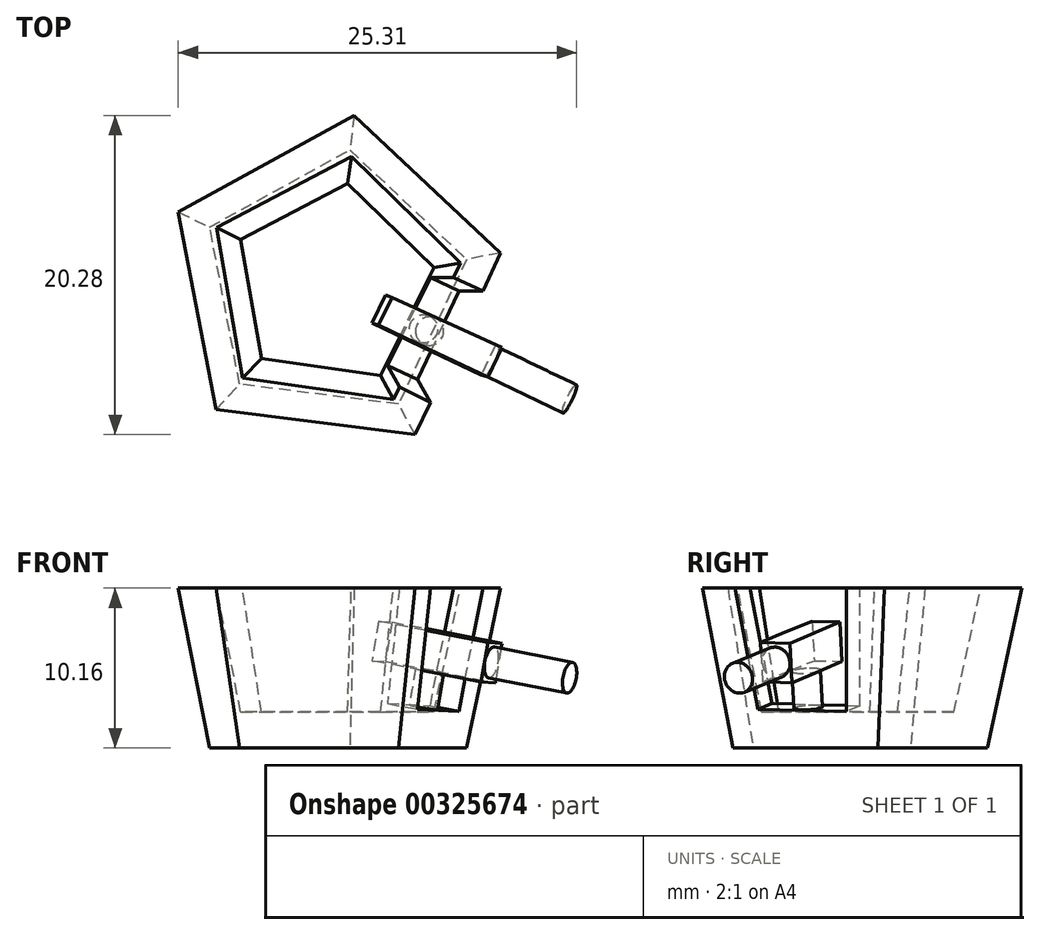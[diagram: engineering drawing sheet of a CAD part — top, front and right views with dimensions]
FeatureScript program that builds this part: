
annotation { "Feature Type Name" : "Feature", "Feature Type Description" : "" }
export const myFeature = defineFeature(function(context is Context, id is Id, definition is map)
    precondition{}
    {
        {
            var Q0;
            Q0=qCreatedBy(makeId("Top.planeOp"),FACE);
            var sketch = newSketch(context, id + "F0", { "sketchPlane" : qUnion([Q0])});
            skCircle(sketch, "E0.cCircle", {"center": v(0, 0) * mm, "radius": 7 * mm, "construction": true});
            skLineSegment(sketch, "E0.0", {"start": v(-7.82, 3.68) * mm, "end": v(1.08, 8.57) * mm});
            skLineSegment(sketch, "E0.1", {"start": v(1.08, 8.57) * mm, "end": v(8.49, 1.62) * mm});
            skLineSegment(sketch, "E0.2", {"start": v(8.49, 1.62) * mm, "end": v(4.17, -7.57) * mm});
            skLineSegment(sketch, "E0.3", {"start": v(4.17, -7.57) * mm, "end": v(-5.91, -6.3) * mm});
            skLineSegment(sketch, "E0.4", {"start": v(-5.91, -6.3) * mm, "end": v(-7.82, 3.68) * mm});
            skPoint(sketch, "E0.0.midPoint", {"position": v(-3.37, 6.13) * mm});
            skSolve(sketch);
        }
        {
            var Q0;
            Q0=makeQuery(id+"F0.imprint","IMPRINT",FACE,{"disambiguationData":[TD([[makeQuery(id+"F0.imprint","IMPRINT",EDGE,{"derivedFrom":sQuery(id+"F0.wireOp",EDGE,"E0.0")}),-1.0]])]});
            extrude(context, id + "F1", {"entities" : qUnion([Q0]), "depth" : 10.16 * mm, "hasDraft" : true, "draftAngle" : 10 * degree});
        }
        {
            var Q0;
            Q0=makeQuery(id+"F1.opExtrude","CAP_FACE",FACE,{"disambiguationData":[OSD([sQuery(id+"F0.wireOp",EDGE,"E0.0"),sQuery(id+"F0.wireOp",EDGE,"E0.1"),sQuery(id+"F0.wireOp",EDGE,"E0.2"),sQuery(id+"F0.wireOp",EDGE,"E0.3"),sQuery(id+"F0.wireOp",EDGE,"E0.4")])],"isStart":false});
            var sketch = newSketch(context, id + "F2", { "sketchPlane" : qUnion([Q0])});
            skCircle(sketch, "E1.cCircle", {"center": v(0, 0) * mm, "radius": 6.66 * mm, "construction": true});
            skLineSegment(sketch, "E1.0", {"start": v(1.17, 8.15) * mm, "end": v(8.11, 1.4) * mm});
            skLineSegment(sketch, "E1.1", {"start": v(8.11, 1.4) * mm, "end": v(3.84, -7.28) * mm});
            skLineSegment(sketch, "E1.2", {"start": v(3.84, -7.28) * mm, "end": v(-5.74, -5.9) * mm});
            skLineSegment(sketch, "E1.3", {"start": v(-5.74, -5.9) * mm, "end": v(-7.39, 3.63) * mm});
            skLineSegment(sketch, "E1.4", {"start": v(-7.39, 3.63) * mm, "end": v(1.17, 8.15) * mm});
            skPoint(sketch, "E1.0.midPoint", {"position": v(4.64, 4.78) * mm});
            skSolve(sketch);
        }
        {
            var Q0;
            Q0=makeQuery(id+"F2.imprint","IMPRINT",FACE,{"disambiguationData":[TD([[makeQuery(id+"F2.imprint","IMPRINT",EDGE,{"derivedFrom":sQuery(id+"F2.wireOp",EDGE,"E1.0")}),-1.0]])]});
            extrude(context, id + "F3", {"entities" : qUnion([Q0]), "operationType" : NewBodyOperationType.REMOVE, "oppositeDirection" : true, "depth" : 7.87 * mm, "hasDraft" : true, "draftAngle" : 10 * degree, "draftPullDirection" : true});
        }
        {
            var Q0;
            Q0=makeQuery(id+"F1.opExtrude","SWEPT_FACE",FACE,{"disambiguationData":[OSD([sQuery(id+"F0.wireOp",EDGE,"E0.2")])]});
            var sketch = newSketch(context, id + "F4", { "sketchPlane" : qUnion([Q0])});
            skLineSegment(sketch, "E2", {"start": v(-5.64, 13.98) * mm, "end": v(-3.44, 3.45) * mm});
            skLineSegment(sketch, "E3", {"start": v(-3.44, 3.45) * mm, "end": v(2.76, 3.83) * mm});
            skLineSegment(sketch, "E4", {"start": v(2.76, 3.83) * mm, "end": v(2.76, 14.1) * mm});
            skLineSegment(sketch, "E5", {"start": v(2.76, 14.1) * mm, "end": v(-5.64, 13.98) * mm});
            skSolve(sketch);
        }
        {
            var Q0;
            {var subQ0=sQuery(id+"F4.wireOp",EDGE,"E3");Q0=makeQuery(id+"F4.imprint","IMPRINT",FACE,{"disambiguationData":[TD([[makeQuery(id+"F4.imprint","IMPRINT",EDGE,{"derivedFrom":subQ0}),1.0]])]});}
            extrude(context, id + "F5", {"entities" : qUnion([Q0]), "operationType" : NewBodyOperationType.REMOVE, "oppositeDirection" : true, "depth" : 9.9 * mm});
        }
        {
            var Q0;
            Q0=makeQuery(id+"F5.boolean.opBoolean","COPY",FACE,{"derivedFrom":makeQuery(id+"F5.opExtrude","SWEPT_FACE",FACE,{"disambiguationData":[OSD([sQuery(id+"F4.wireOp",EDGE,"E3")])]})});
            var sketch = newSketch(context, id + "F6", { "sketchPlane" : qUnion([Q0])});
            skCircle(sketch, "E6", {"center": v(5.22, -2.65) * mm, "radius": 0.9 * mm});
            skSolve(sketch);
        }
        {
            var Q0;
            Q0=makeQuery(id+"F6.imprint","IMPRINT",FACE,{"disambiguationData":[TD([[makeQuery(id+"F6.imprint","IMPRINT",EDGE,{"derivedFrom":sQuery(id+"F6.wireOp",EDGE,"E6")}),1.0]])]});
            extrude(context, id + "F7", {"entities" : qUnion([Q0]), "operationType" : NewBodyOperationType.ADD, "depth" : 2.36 * mm});
        }
        {
            var Q0;
            Q0=makeQuery(id+"F7.opExtrude","CAP_FACE",FACE,{"disambiguationData":[OSD([sQuery(id+"F6.wireOp",EDGE,"E6")])],"isStart":false});
            var sketch = newSketch(context, id + "F8", { "sketchPlane" : qUnion([Q0])});
            skLineSegment(sketch, "E7", {"start": v(4.73, -3.66) * mm, "end": v(1.52, -2.1) * mm});
            skLineSegment(sketch, "E8", {"start": v(1.52, -2.1) * mm, "end": v(2.37, -0.34) * mm});
            skLineSegment(sketch, "E9", {"start": v(2.37, -0.34) * mm, "end": v(9.45, -3.6) * mm});
            skLineSegment(sketch, "E10", {"start": v(9.45, -3.6) * mm, "end": v(8.55, -5.46) * mm});
            skLineSegment(sketch, "E11", {"start": v(8.55, -5.46) * mm, "end": v(4.73, -3.66) * mm});
            skSolve(sketch);
        }
        {
            var Q0;
            {var subQ0=sQuery(id+"F8.wireOp",EDGE,"E9");var subQ1=makeQuery(id+"F7.opExtrude","CAP_EDGE",EDGE,{"disambiguationData":[OSD([sQuery(id+"F6.wireOp",EDGE,"E6")])],"isStart":false});var subQ2=makeQuery(id+"F8.imprint","INTERSECT",VERTEX,{"disambiguationData":[OD(0.0)],"derivedFrom":[subQ1,subQ0]});Q0=makeQuery(id+"F8.imprint","IMPRINT",FACE,{"disambiguationData":[TD([[makeQuery(id+"F8.imprint","IMPRINT",EDGE,{"disambiguationData":[TD([[subQ2,-1.0]])],"derivedFrom":subQ0}),-1.0]])]});}
            var Q1;
            Q1=makeQuery(id+"F8.imprint","IMPRINT",FACE,{"disambiguationData":[TD([[makeQuery(id+"F8.imprint","IMPRINT",EDGE,{"derivedFrom":sQuery(id+"F8.wireOp",EDGE,"E7")}),-1.0]])]});
            extrude(context, id + "F9", {"entities" : qUnion([Q0, Q1]), "operationType" : NewBodyOperationType.ADD, "depth" : 2.54 * mm});
        }
        {
            var Q0;
            Q0=makeQuery(id+"F9.opExtrude","SWEPT_FACE",FACE,{"disambiguationData":[OSD([sQuery(id+"F8.wireOp",EDGE,"E10")])]});
            var sketch = newSketch(context, id + "F10", { "sketchPlane" : qUnion([Q0])});
            skCircle(sketch, "E12", {"center": v(-0.62, 7.27) * mm, "radius": 1 * mm});
            skSolve(sketch);
        }
        {
            var Q0;
            Q0=makeQuery(id+"F10.imprint","IMPRINT",FACE,{"disambiguationData":[TD([[makeQuery(id+"F10.imprint","IMPRINT",EDGE,{"derivedFrom":sQuery(id+"F10.wireOp",EDGE,"E12")}),1.0]])]});
            extrude(context, id + "F11", {"entities" : qUnion([Q0]), "operationType" : NewBodyOperationType.ADD, "depth" : 5.6 * mm});
        }
    });
